# Revit family: Reece_Tap_American Standard_Studio_Sink Mixer_Pull Out Spray_207 mm
name_source: partatom
category: Plumbing Fixtures
revit_build: Autodesk Revit 2018 (Build: 20190510_1515(x64)
units: mm (PartAtom-declared; Revit-internal decimal feet)

## family parameters
Cut with Voids When Loaded = No
Host = Face
Part Type = Normal
Room Calculation Point = Yes
Round Connector Dimension = Use Diameter
Shared = Yes

## types (1)
- Chrome
    CWFU = 0
    Default Elevation = 1000 mm  [stored 3.28084 ft]
    Description = American Standard Studio Saga Sink Mixer Tap with Pull Out Spray (4 Star)
    Disclaimer = THIS FILE IS THE PROPERTY OF THE REECE GROUP. IT MAY NOT BE REPRODUCED, REVERSE-ENGINEERED OR MODIFIED. ANY REPUBLICATION, TRANSMISSION OR DISTRIBUTION FOR THE PURPOSE OF COMMERCIALLY EXPLOITING THE FILES IS PROHIBITED.
    HWFU = 0
    Keynote = Product #9506812, Reece_Tap_American Standard_Studio_Sink Mixer_Pull Out Spray_207 mm - Chrome
    Manufacturer = American Standard
    Model = Studio
    Reece_Detail_Additional = Sink Mixer
    Reece_Detail_Disclaimer = THIS FILE IS THE PROPERTY OF THE REECE GROUP. IT MAY NOT BE REPRODUCED, REVERSE-ENGINEERED OR MODIFIED. ANY REPUBLICATION, TRANSMISSION OR DISTRIBUTION FOR THE PURPOSE OF COMMERCIALLY EXPLOITING THE FILES IS PROHIBITED.
    Reece_Detail_Installation = Pull Out Spray
    Reece_Material-Main = Reece_Brass_Chrome
    Reece_Material_Colour = Reece_Plastic_Grey
    Reece_Material_Secondary = Reece_Plastic_Black
    Reece_Material_Tap_Cold = Render_Cold_Water_Cap
    Reece_Material_Tap_Hot = Render_Hot_Water_Cap
    Reece_Overall_Length = 186 mm  [stored 0.610236 ft]
    Reece_Product_Brand = American Standard
    Reece_Product_Description = American Standard Studio Saga Sink Mixer Tap with Pull Out Spray (4 Star)
    Reece_Product_Mount = Hob Mounted
    Reece_Product_Number = 9506812
    Reece_Product_Sub Brand = Studio
    Reece_Product_Type = Tap
    Reece_Product_Web Page = https://www.reece.com.au
    Reece_Tap_Clearance = 130 mm  [stored 0.426509 ft]
    Reece_Tap_Inlet = 13 mm
    Reece_Tap_Reach = 207 mm  [stored 0.679134 ft]
    Type Comments = Tap
    URL = https://www.reece.com.au
    WFU = 0

note: [stored X ft] marks values corroborated as IEEE doubles in the binary element streams (Revit-internal decimal feet)

## geometry (parser evidence)
native form markers: Sweep x2
no freeform markers — native parametric forms only
